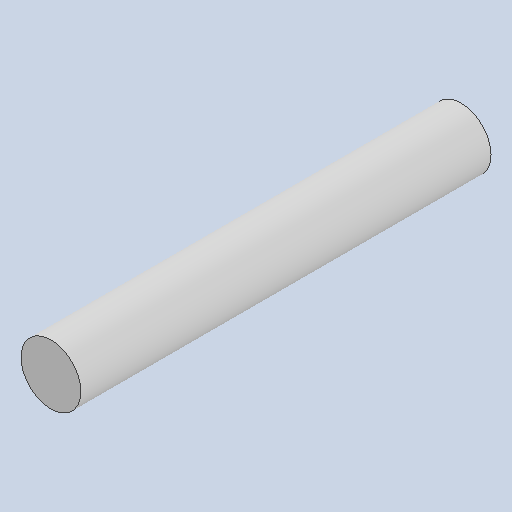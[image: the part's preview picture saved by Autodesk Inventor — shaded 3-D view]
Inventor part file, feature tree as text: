
AUTODESK INVENTOR PART (.ipt)
format: ipt  version: 2024.3 (Build 283343000, 343)  size: 135,680 bytes
history: native  units: mm
features: other x2, extrude x1, sketch x1, reference x1
ambient origin geometry x8: Origin, YZ Plane, XZ Plane, XY Plane, X Axis, Y Axis, Z Axis, Center Point
bodies: Solid1 (feature_tree)
feature tree (5):
  extrude  "Extrusion1"  [1 undecoded]
  sketch  "Sketch1"  dims[d0=26.0mm d1=0.0mm]
  reference  "Reference1"
  other  "Assembly1"
  other  "housing:1"
note: 1 required parameter value undecoded (feature->parameter linkage not recoverable at this tier; creation-order binding heuristic only, values carry confidence <= 0.55)
